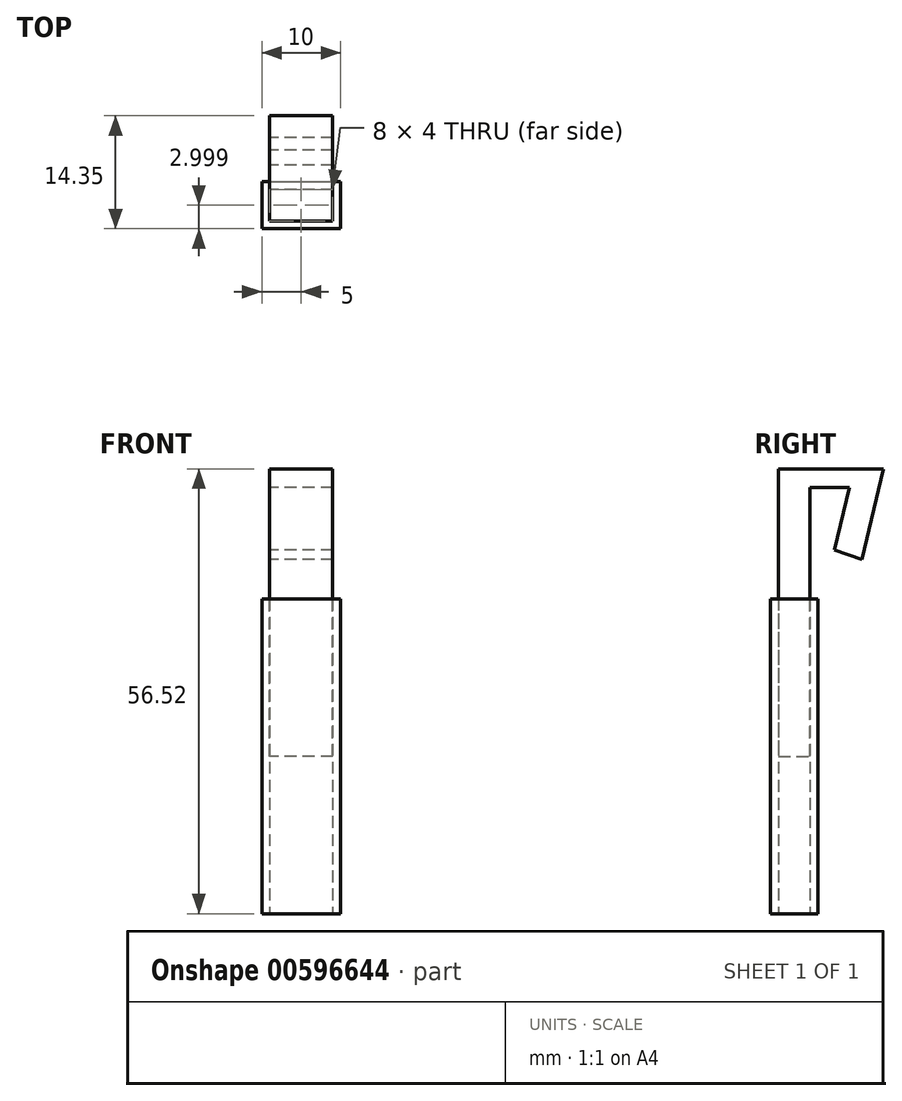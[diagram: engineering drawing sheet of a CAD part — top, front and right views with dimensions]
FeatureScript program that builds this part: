
annotation { "Feature Type Name" : "Feature", "Feature Type Description" : "" }
export const myFeature = defineFeature(function(context is Context, id is Id, definition is map)
    precondition{}
    {
        {
            var Q0;
            Q0=qCreatedBy(makeId("Right.planeOp"),FACE);
            var sketch = newSketch(context, id + "F0", { "sketchPlane" : qUnion([Q0])});
            skLineSegment(sketch, "E0", {"start": v(-32.63, 22.65) * mm, "end": v(-27.63, 22.65) * mm});
            skLineSegment(sketch, "E1", {"start": v(-36.63, 25.04) * mm, "end": v(-36.63, -11.48) * mm});
            skLineSegment(sketch, "E2", {"start": v(-36.63, -11.48) * mm, "end": v(-32.63, -11.48) * mm});
            skLineSegment(sketch, "E3", {"start": v(-32.63, -11.48) * mm, "end": v(-32.63, 22.65) * mm});
            skLineSegment(sketch, "E4", {"start": v(-26.63, 8.04) * mm, "end": v(-32.63, 8.04) * mm, "construction": true});
            skLineSegment(sketch, "E5", {"start": v(-27.63, 22.65) * mm, "end": v(-29.52, 14.71) * mm});
            skLineSegment(sketch, "E6", {"start": v(-36.63, 25.04) * mm, "end": v(-23.28, 25.04) * mm});
            skLineSegment(sketch, "E7", {"start": v(-23.28, 25.04) * mm, "end": v(-26.02, 13.53) * mm});
            skLineSegment(sketch, "E8", {"start": v(-26.02, 13.53) * mm, "end": v(-29.52, 14.71) * mm});
            skSolve(sketch);
        }
        {
            var Q0;
            Q0 = qSketchRegion(id + "F0", true);
            extrude(context, id + "F1", {"entities" : qUnion([Q0]), "depth" : 8 * mm, "offsetDistance" : 25 * mm});
        }
        {
            var Q0;
            Q0=makeQuery(id+"F1.opExtrude","SWEPT_FACE",FACE,{"disambiguationData":[OSD([sQuery(id+"F0.wireOp",EDGE,"E2")])]});
            var sketch = newSketch(context, id + "F2", { "sketchPlane" : qUnion([Q0])});
            skLineSegment(sketch, "E9.0", {"start": v(-1, 37.63) * mm, "end": v(-1, 31.63) * mm});
            skLineSegment(sketch, "E9.1", {"start": v(9, 37.63) * mm, "end": v(-1, 37.63) * mm});
            skLineSegment(sketch, "E9.2", {"start": v(9, 31.63) * mm, "end": v(9, 37.63) * mm});
            skLineSegment(sketch, "E9.3", {"start": v(-1, 31.63) * mm, "end": v(9, 31.63) * mm});
            skLineSegment(sketch, "E10.bottom", {"start": v(0, 32.63) * mm, "end": v(8, 32.63) * mm});
            skLineSegment(sketch, "E10.top", {"start": v(0, 36.63) * mm, "end": v(8, 36.63) * mm});
            skLineSegment(sketch, "E10.left", {"start": v(0, 32.63) * mm, "end": v(0, 36.63) * mm});
            skLineSegment(sketch, "E10.right", {"start": v(8, 32.63) * mm, "end": v(8, 36.63) * mm});
            skSolve(sketch);
        }
        {
            var Q0;
            Q0 = qSketchRegion(id + "F2", true);
            extrude(context, id + "F3", {"entities" : qUnion([Q0]), "endBound" : BoundingType.SYMMETRIC, "oppositeDirection" : true, "depth" : 40 * mm, "offsetDistance" : 25 * mm});
        }
    });
